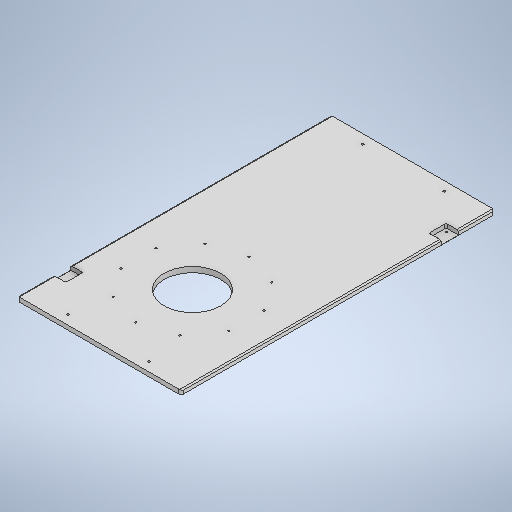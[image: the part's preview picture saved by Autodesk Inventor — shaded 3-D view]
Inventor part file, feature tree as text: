
AUTODESK INVENTOR PART (.ipt)
format: ipt  version: 2025 (Build 290162000, 162)  size: 414,208 bytes
history: native  units: in
note: dims shown in document units (in); Inventor stores cm internally (conversion verified against a paired STEP export)
features: sketch x9, extrude x5, hole x3, chamfer x3, plane x2, fillet x2, pattern_circular x1
ambient origin geometry x8: Origin, YZ Plane, XZ Plane, XY Plane, X Axis, Y Axis, Z Axis, Center Point
bodies: Solid1 (feature_tree)
feature tree (25):
  extrude  "Base Cover"  Depth=27.1654in
  sketch  "Sketch2"  dims[d2=0.4724in d3=0.0in d4=8.0709in]
  extrude  "Cylinder Hole"  Depth=0.4724in
  plane  "Work Plane1"
  hole  "Handle Holes"  [1 undecoded]
  sketch  "Sketch7"  dims[d8=10.6299in d50=5.9055in d55=7.0625in]
  plane  "Work Plane2"
  hole  "Cylinder Mount Holes"  [1 undecoded]
  sketch  "Sketch9"  dims[d57=0.1936in d58=0.1969in d59=0.1575in d60=0.0787in d61=90.0deg d62=0.1969in d63=0.8108in]
  fillet  "Rounded Side Corners"  Radius=7.0625in
  chamfer  "Chamfer1"  Distance=1.063in
  chamfer  "Chamfer2"  Distance=1.063in
  extrude  "Magnet Seats"  Depth=0.3937in
  hole  "Magnet Holes"  [1 undecoded]
  chamfer  "Chamfer5"  Distance=3.1102in
  fillet  "Rounded Bottom Corners"  Radius=3.1102in
  extrude  "Extrusion14"  Depth=0.3937in
  extrude  "Extrusion15"  Depth=0.3937in TaperAngle=45.0deg
  pattern_circular  "Circular Pattern1"  Angle=45.0deg  [1 undecoded]
  sketch  "Sketch1"  dims[d0=14.1732in d1=27.1654in]
  sketch  "Sketch6"  dims[d5=4.9107in d6=0.0in d7=0.0in]
  sketch  "Sketch8"  dims[d56=25.5906in]
  sketch  "Sketch11"  dims[d64=10.3543in]
  sketch  "Sketch18"  dims[d65=10.6299in]
  sketch  "Sketch19"  dims[d68=9.8425in d74=0.1628in d75=0.3937in d76=0.1575in d77=0.0787in d78=90.0deg d79=0.3937in d80=0.8108in d82=1.063in d83=1.063in d84=1.4961in d85=1.4961in d86=3.1102in d87=3.1102in d88=0.1969in d89=0.0984in d90=0.0787in d91=45.0deg d92=0.0984in d93=0.0787in d94=45.0deg d95=0.1181in d96=0.1181in d97=0.3543in d98=0.0in d109=0.748in d110=0.315in d111=0.8661in d112=0.748in d113=0.1299in d114=0.1299in d115=0.1299in d116=0.1299in d118=0.315in d119=0.8661in d120=0.748in d121=0.748in d122=0.1276in d123=0.315in d124=0.1575in d125=0.0787in d126=90.0deg d127=0.315in d128=0.8108in d129=0.0138in d130=0.0787in d131=45.0deg d230=0.2756in d243=0.1378in d244=0.0787in d245=0.3848in d246=0.0in d247=0.1378in d248=0.0787in d249=0.3937in d250=0.0in d278=0.1575in d279=3.937in d280=360.0deg d26=0.0394in d27=0.0394in d28=0.0394in d29=0.0059in d30=0.0098in d31=0.0148in d32=0.5635in d33=0.0295in d34=0.8108in d35=0.0025in d36=0.0295in d37=0.0148in d66=0.0197in d67=0.0344in d251=0.0394in d252=0.0394in d253=0.0394in d254=0.0059in d255=0.0098in d256=0.0148in d257=0.5635in d258=0.0295in d259=0.8108in d260=0.0025in d261=0.0295in d262=0.0148in d263=0.0394in d264=0.0394in d265=0.0059in d266=0.0098in d267=0.0148in d268=0.5635in d269=0.0295in d270=0.8108in d271=0.0025in d272=0.0295in d273=0.0148in]
note: 4 required parameter values undecoded (feature->parameter linkage not recoverable at this tier; creation-order binding heuristic only, values carry confidence <= 0.55)
